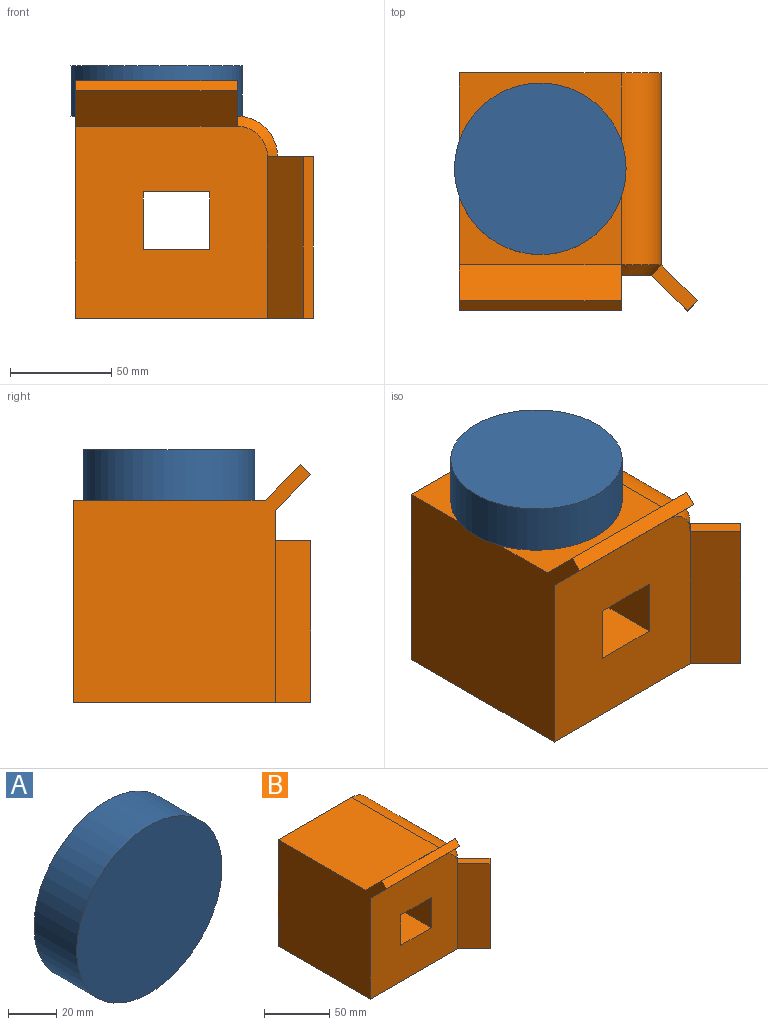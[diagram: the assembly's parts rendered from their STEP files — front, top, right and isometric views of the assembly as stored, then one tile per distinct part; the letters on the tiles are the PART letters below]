
ASSEMBLY  parts=2 mates=1
PART A: 3 faces, bbox 84.9x25x84.9 mm
  f0: cylinder r=42.44mm len=84.89mm, axis (0,1,0), area 6667.2mm2, adj f1,f2
  f1: plane 84.89x84.89mm, normal (0,-1,0), area 5659.7mm2, adj f0
  f2: plane 84.89x84.89mm, normal (0,1,0), area 5659.7mm2, adj f0
PART B: 22 faces, bbox 117.7x117.7x117.7 mm
  f0: plane 117.68x117.68mm, normal (-1,0,0), area 10164.3mm2, adj f1,f6,f7,f8,f18,f20,f21
  f1: plane 117.68x117.68mm, normal (0,0,-1), area 7789.3mm2, adj f0,f7,f8,f12,f13,f15,f16,f17
  f2: plane 100x32.86mm, normal (0,0,1), area 3286mm2, adj f3,f5,f7,f8
  f3: plane 100x28.54mm, normal (1,0,0), area 2853.6mm2, adj f2,f4,f7,f8
  f4: plane 100x32.86mm, normal (0,0,-1), area 3286mm2, adj f3,f5,f7,f8
  f5: plane 100x28.54mm, normal (-1,0,0), area 2853.6mm2, adj f2,f4,f7,f8
  f6: plane 95x80mm, normal (0,0,1), area 7600mm2, adj f0,f8,f9,f20
  f7: plane 95x95mm, normal (0,-1,0), area 8039mm2, adj f0,f1,f2,f3,f4,f5,f10,f15
  f8: plane 100x100mm, normal (0,1,0), area 6976.5mm2, adj f0,f1,f2,f3,f4,f5,f6,f9
  f9: cylinder r=20mm len=95mm, axis (0,1,0), area 2984.5mm2, adj f6,f8,f10,f11
  f10: cone r=15mm half-angle=45deg, axis (0,1,0), area 194.4mm2, adj f7,f9,f14,f19
  f11: plane 95x25mm, normal (0,0,-1), area 2375mm2, adj f8,f9,f12,f13
  f12: plane 80x25mm, normal (0,1,0), area 2000mm2, adj f1,f11,f13,f16
  f13: plane 95x80mm, normal (1,0,0), area 7600mm2, adj f1,f8,f11,f12
  f14: plane 22.68x22.68mm, normal (0,0,1), area 176.8mm2, adj f10,f15,f16,f17
  f15: plane 80x17.68mm, normal (-0.71,-0.71,0), area 2000mm2, adj f1,f7,f14,f17
  f16: plane 80x17.68mm, normal (0.71,0.71,0), area 2000mm2, adj f1,f12,f14,f17
  f17: plane 80x5mm, normal (0.71,-0.71,0), area 565.7mm2, adj f1,f14,f15,f16
  f18: plane 80x17.68mm, normal (0,-0.71,-0.71), area 2000mm2, adj f0,f7,f19,f21
  f19: plane 22.68x22.68mm, normal (1,0,0), area 176.8mm2, adj f10,f18,f20,f21
  f20: plane 80x17.68mm, normal (0,0.71,0.71), area 2000mm2, adj f0,f6,f19,f21
  f21: plane 80x5mm, normal (0,-0.71,0.71), area 565.7mm2, adj f0,f18,f19,f20
PLACE A rot(axis=(1,0,0),90deg) t=(-85.6,9.51,122.11)mm
PLACE B t=(-125.63,25.27,-27.47)mm
MATE fastened A.f0 <-> B.f6  axis (0,0,-1) through (-141.59,-22.23,97.11)mm
